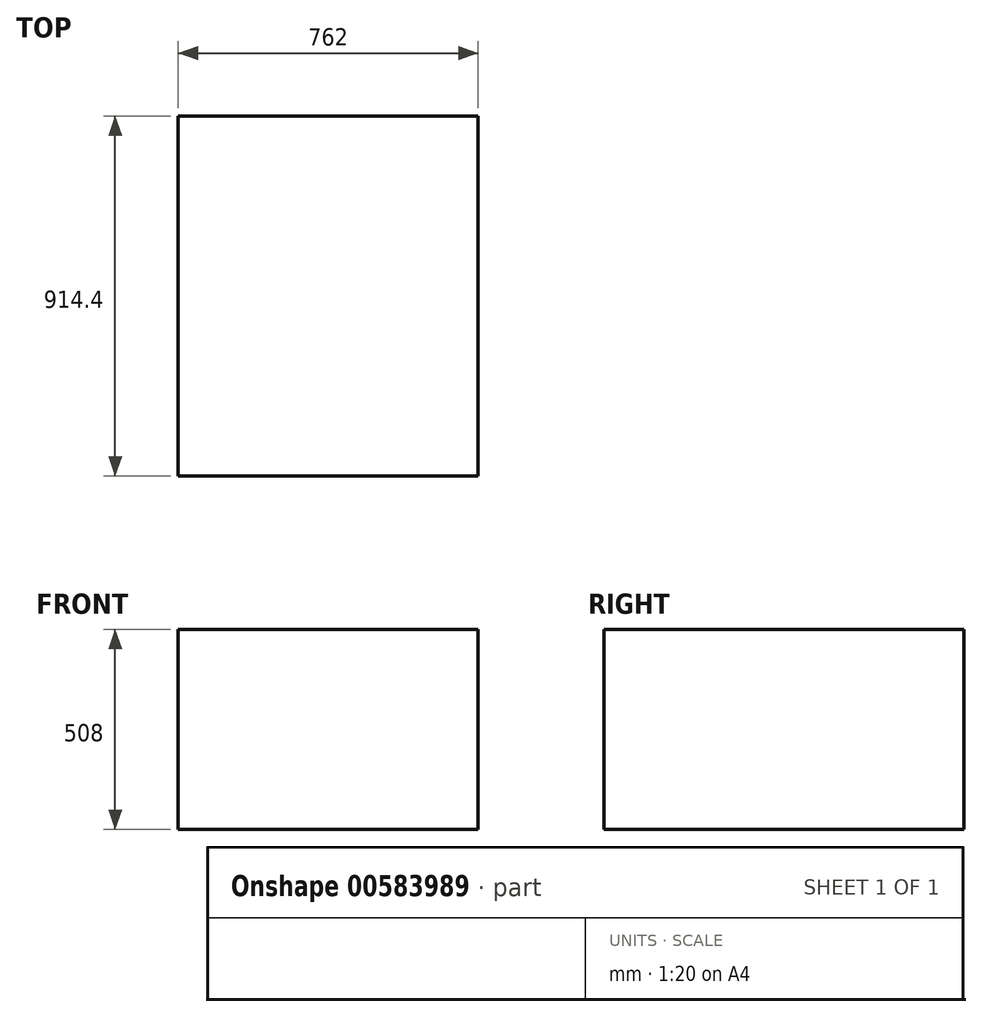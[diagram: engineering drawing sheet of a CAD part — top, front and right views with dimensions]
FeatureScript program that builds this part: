
annotation { "Feature Type Name" : "Feature", "Feature Type Description" : "" }
export const myFeature = defineFeature(function(context is Context, id is Id, definition is map)
    precondition{}
    {
        {
            var Q0;
            Q0=qCreatedBy(makeId("Top.planeOp"),FACE);
            var sketch = newSketch(context, id + "F0", { "sketchPlane" : qUnion([Q0])});
            skLineSegment(sketch, "E0.bottom", {"start": v(-390.44, 754.18) * mm, "end": v(371.56, 754.18) * mm});
            skLineSegment(sketch, "E0.top", {"start": v(-390.44, -160.22) * mm, "end": v(371.56, -160.22) * mm});
            skLineSegment(sketch, "E0.left", {"start": v(-390.44, 754.18) * mm, "end": v(-390.44, -160.22) * mm});
            skLineSegment(sketch, "E0.right", {"start": v(371.56, 754.18) * mm, "end": v(371.56, -160.22) * mm});
            skSolve(sketch);
        }
        {
            var Q0;
            Q0=makeQuery(id+"F0.imprint","IMPRINT",FACE,{"disambiguationData":[TD([[makeQuery(id+"F0.imprint","IMPRINT",EDGE,{"derivedFrom":sQuery(id+"F0.wireOp",EDGE,"E0.bottom")}),-1.0]])]});
            extrude(context, id + "F1", {"entities" : qUnion([Q0]), "depth" : 508 * mm, "offsetDistance" : 25.4 * mm});
        }
    });
